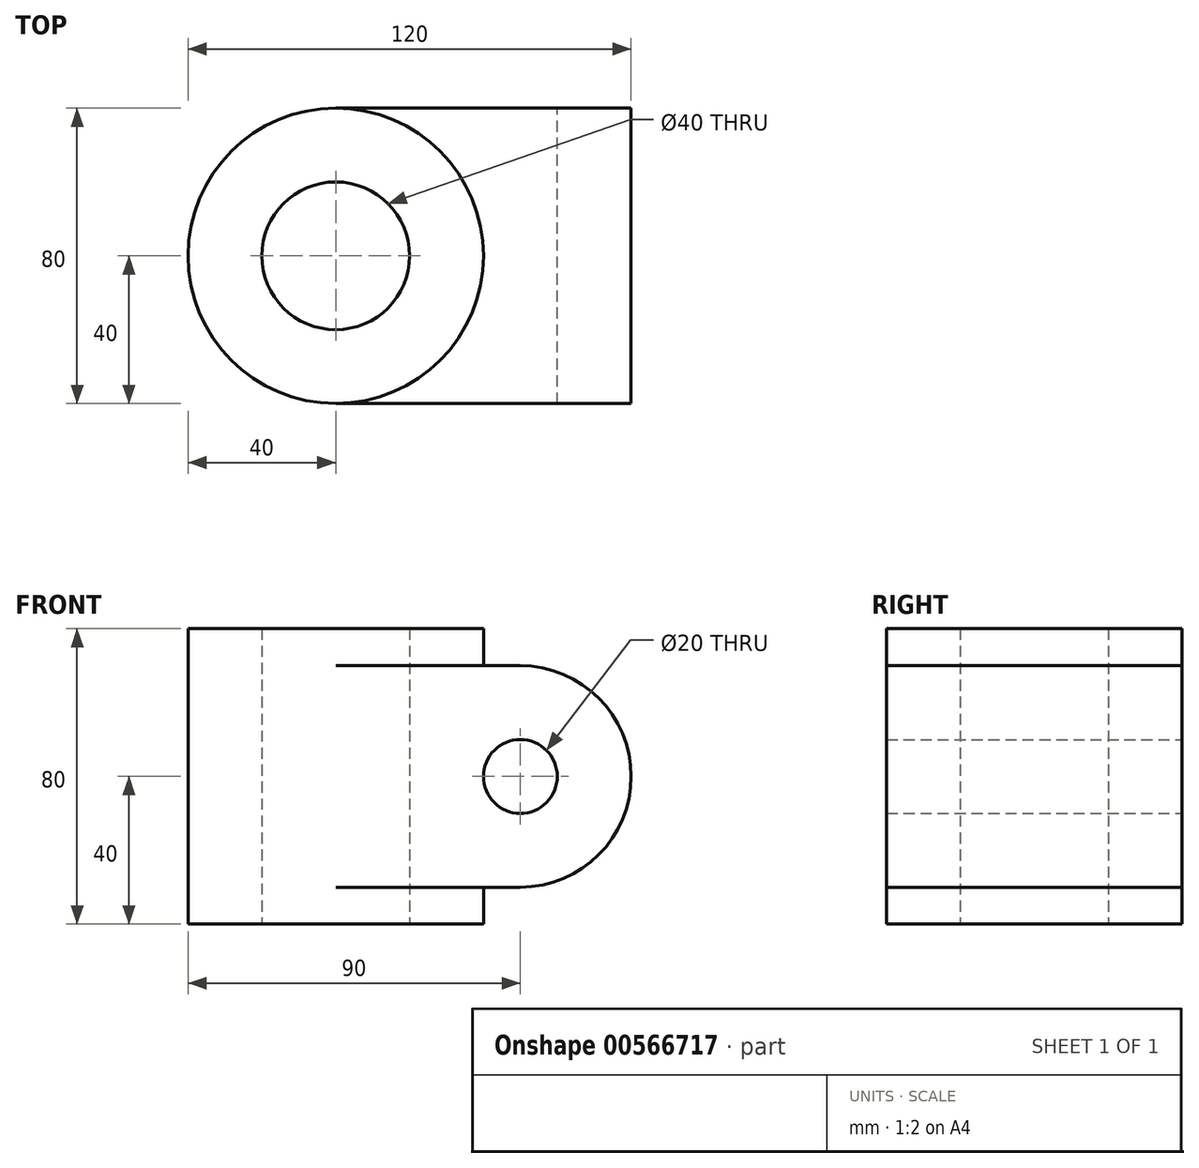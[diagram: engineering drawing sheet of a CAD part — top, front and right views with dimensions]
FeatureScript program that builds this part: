
annotation { "Feature Type Name" : "Feature", "Feature Type Description" : "" }
export const myFeature = defineFeature(function(context is Context, id is Id, definition is map)
    precondition{}
    {
        {
            var Q0;
            Q0=qCreatedBy(makeId("Top.planeOp"),FACE);
            var sketch = newSketch(context, id + "F0", { "sketchPlane" : qUnion([Q0])});
            skCircle(sketch, "E0", {"center": v(0, 0) * mm, "radius": 40 * mm});
            skCircle(sketch, "E1", {"center": v(0, 0) * mm, "radius": 20 * mm});
            skSolve(sketch);
        }
        {
            var Q0;
            Q0=makeQuery(id+"F0.imprint","IMPRINT",FACE,{"disambiguationData":[TD([[makeQuery(id+"F0.imprint","IMPRINT",EDGE,{"derivedFrom":sQuery(id+"F0.wireOp",EDGE,"E0")}),1.0]])]});
            extrude(context, id + "F1", {"entities" : qUnion([Q0]), "endBound" : BoundingType.SYMMETRIC, "depth" : 80 * mm, "offsetDistance" : 25 * mm});
        }
        {
            var Q0;
            Q0=qCreatedBy(makeId("Front.planeOp"),FACE);
            var sketch = newSketch(context, id + "F2", { "sketchPlane" : qUnion([Q0])});
            skLineSegment(sketch, "E2.bottom", {"start": v(0, 30) * mm, "end": v(50, 30) * mm});
            skLineSegment(sketch, "E2.top", {"start": v(0, -30) * mm, "end": v(50, -30) * mm});
            skLineSegment(sketch, "E2.left", {"start": v(0, 30) * mm, "end": v(0, -30) * mm});
            skLineSegment(sketch, "E2.right", {"start": v(80, 0) * mm, "end": v(80, 0) * mm});
            skPoint(sketch, "E3.visualSharp", {"position": v(80, 30) * mm});
            skArc(sketch, "E3.filletArc", {"start": v(80, 0) * mm, "mid": v(71.21, 21.21) * mm, "end": v(50, 30) * mm});
            skPoint(sketch, "E4.visualSharp", {"position": v(80, -30) * mm});
            skArc(sketch, "E4.filletArc", {"start": v(50, -30) * mm, "mid": v(71.21, -21.21) * mm, "end": v(80, 0) * mm});
            skCircle(sketch, "E5", {"center": v(50, 0) * mm, "radius": 10 * mm});
            skSolve(sketch);
        }
        {
            var Q0;
            Q0 = qSketchRegion(id + "F2", true);
            extrude(context, id + "F3", {"entities" : qUnion([Q0]), "operationType" : NewBodyOperationType.ADD, "endBound" : BoundingType.SYMMETRIC, "depth" : 80 * mm, "offsetDistance" : 25 * mm});
        }
        {
            var Q0;
            Q0=makeQuery(id+"F3.boolean.opBoolean","SPLIT",FACE,{"disambiguationData":[TD([makeQuery(id+"F1.opExtrude","SWEPT_FACE",FACE,{"disambiguationData":[OSD([sQuery(id+"F0.wireOp",EDGE,"E1")])]})])],"derivedFrom":makeQuery(id+"F3.opExtrude","SWEPT_FACE",FACE,{"disambiguationData":[OSD([sQuery(id+"F2.wireOp",EDGE,"E2.bottom")])]})});
            extrude(context, id + "F4", {"entities" : qUnion([Q0]), "operationType" : NewBodyOperationType.REMOVE, "endBound" : BoundingType.THROUGH_ALL, "oppositeDirection" : true, "depth" : 25 * mm, "offsetDistance" : 25 * mm});
        }
    });
